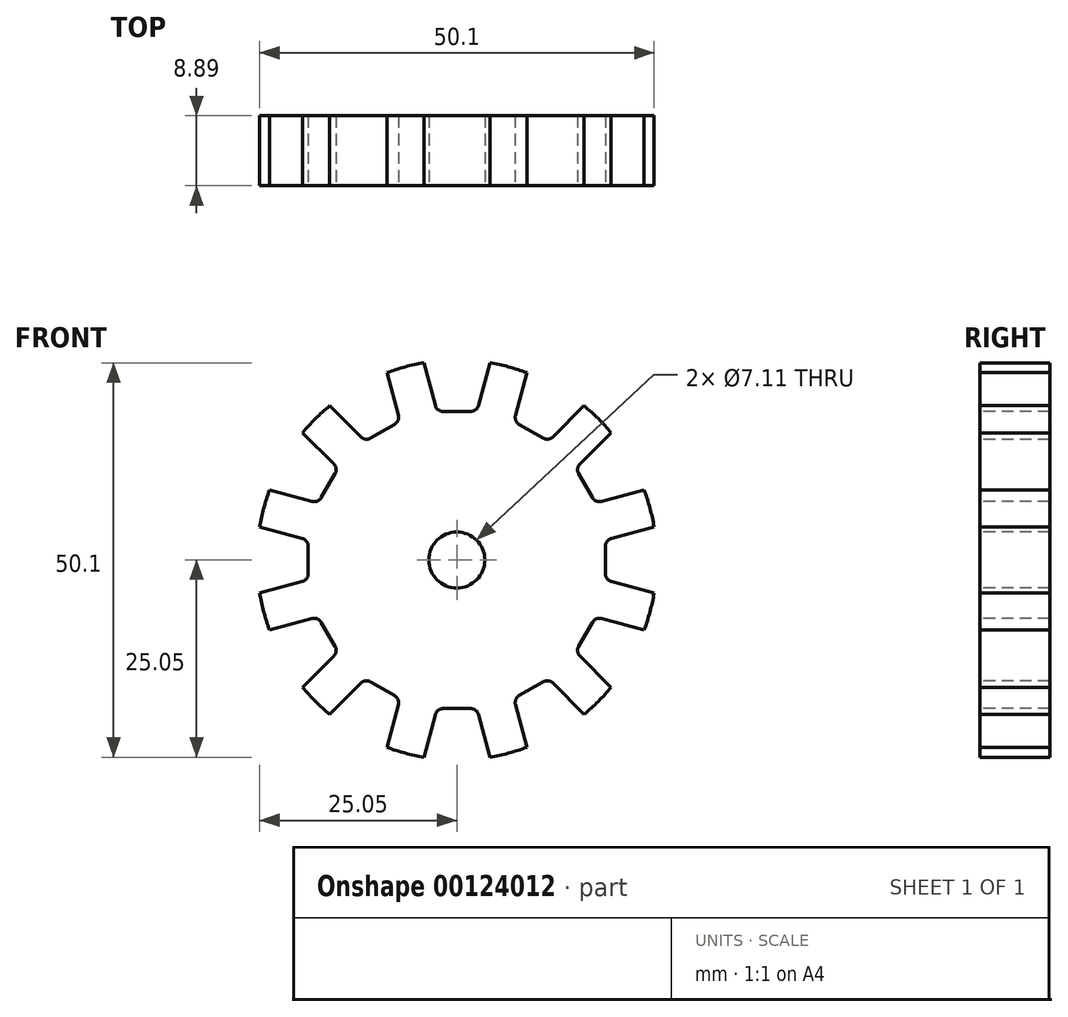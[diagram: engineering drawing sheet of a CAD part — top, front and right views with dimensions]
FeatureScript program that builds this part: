
annotation { "Feature Type Name" : "Feature", "Feature Type Description" : "" }
export const myFeature = defineFeature(function(context is Context, id is Id, definition is map)
    precondition{}
    {
        {
            var Q0;
            Q0=qCreatedBy(makeId("Front.planeOp"),FACE);
            var sketch = newSketch(context, id + "F0", { "sketchPlane" : qUnion([Q0])});
            skCircle(sketch, "E0", {"center": v(0, 0) * mm, "radius": 25.4 * mm});
            skSolve(sketch);
        }
        {
            var Q0;
            Q0 = qSketchRegion(id + "F0", true);
            extrude(context, id + "F1", {"entities" : qUnion([Q0]), "depth" : 8.9 * mm});
        }
        {
            var Q0;
            Q0=makeQuery(id+"F1.opExtrude","CAP_FACE",FACE,{"disambiguationData":[OSD([sQuery(id+"F0.wireOp",EDGE,"E0")])],"isStart":false});
            var sketch = newSketch(context, id + "F2", { "sketchPlane" : qUnion([Q0])});
            skLineSegment(sketch, "E1", {"start": v(0, 0) * mm, "end": v(0, 25.4) * mm, "construction": true});
            skCircle(sketch, "E2", {"center": v(0, 0) * mm, "radius": 19.05 * mm, "construction": true});
            skLineSegment(sketch, "E3", {"start": v(2.74, 19.63) * mm, "end": v(4.2, 25.05) * mm});
            skLineSegment(sketch, "E4", {"start": v(-2.74, 19.63) * mm, "end": v(-4.2, 25.05) * mm});
            skLineSegment(sketch, "E5", {"start": v(-1.76, 18.88) * mm, "end": v(0, 18.88) * mm});
            skLineSegment(sketch, "E6", {"start": v(1.76, 18.88) * mm, "end": v(0, 18.88) * mm});
            skPoint(sketch, "E7.visualSharp", {"position": v(2.54, 18.88) * mm});
            skArc(sketch, "E7.filletArc", {"start": v(1.76, 18.88) * mm, "mid": v(2.38, 19.09) * mm, "end": v(2.74, 19.63) * mm});
            skPoint(sketch, "E8.visualSharp", {"position": v(-2.54, 18.88) * mm});
            skArc(sketch, "E8.filletArc", {"start": v(-2.74, 19.63) * mm, "mid": v(-2.38, 19.09) * mm, "end": v(-1.76, 18.88) * mm});
            skSolve(sketch);
        }
        {
            var Q0;
            {var subQ1=sQuery(id+"F2.wireOp",EDGE,"E3");Q0=makeQuery(id+"F2.imprint","IMPRINT",FACE,{"disambiguationData":[TD([[makeQuery(id+"F2.imprint","IMPRINT",EDGE,{"derivedFrom":subQ1}),1.0]])]});}
            extrude(context, id + "F3", {"entities" : qUnion([Q0]), "operationType" : NewBodyOperationType.REMOVE, "oppositeDirection" : true, "depth" : 25.4 * mm});
        }
        {
            var Q0;
            Q0=makeQuery(id+"F1.opExtrude","SWEPT_BODY",BODY,{"disambiguationData":[OSD([sQuery(id+"F0.wireOp",EDGE,"E0")])]});
            var Q1;
            Q1=makeQuery(id+"F3.boolean.opBoolean","COPY",FACE,{"derivedFrom":makeQuery(id+"F3.opExtrude","SWEPT_FACE",FACE,{"disambiguationData":[OSD([sQuery(id+"F2.wireOp",EDGE,"E4")])]})});
            var Q2;
            Q2=makeQuery(id+"F3.boolean.opBoolean","COPY",FACE,{"derivedFrom":makeQuery(id+"F3.opExtrude","SWEPT_FACE",FACE,{"disambiguationData":[OSD([sQuery(id+"F2.wireOp",EDGE,"E8.filletArc")])]})});
            var Q3;
            Q3=makeQuery(id+"F3.boolean.opBoolean","COPY",FACE,{"derivedFrom":makeQuery(id+"F3.opExtrude","SWEPT_FACE",FACE,{"disambiguationData":[OSD([sQuery(id+"F2.wireOp",EDGE,"E5"),sQuery(id+"F2.wireOp",EDGE,"E6")])]})});
            var Q4;
            Q4=makeQuery(id+"F3.boolean.opBoolean","COPY",FACE,{"derivedFrom":makeQuery(id+"F3.opExtrude","SWEPT_FACE",FACE,{"disambiguationData":[OSD([sQuery(id+"F2.wireOp",EDGE,"E7.filletArc")])]})});
            var Q5;
            Q5=makeQuery(id+"F3.boolean.opBoolean","COPY",FACE,{"derivedFrom":makeQuery(id+"F3.opExtrude","SWEPT_FACE",FACE,{"disambiguationData":[OSD([sQuery(id+"F2.wireOp",EDGE,"E3")])]})});
            var Q6;
            Q6=makeQuery(id+"F1.opExtrude","SWEPT_FACE",FACE,{"disambiguationData":[OSD([sQuery(id+"F0.wireOp",EDGE,"E0")])]});
            circularPattern(context, id + "F4", {"patternType" : PatternType.FACE, "faces" : qUnion([Q1, Q2, Q3, Q4, Q5]), "axis" : qUnion([Q6]), "angle" : 30 * degree, "instanceCount" : 12});
        }
        {
            var Q0;
            Q0=makeQuery(id+"F1.opExtrude","CAP_FACE",FACE,{"disambiguationData":[OSD([sQuery(id+"F0.wireOp",EDGE,"E0")])],"isStart":false});
            var sketch = newSketch(context, id + "F5", { "sketchPlane" : qUnion([Q0])});
            skCircle(sketch, "E9", {"center": v(0, 0) * mm, "radius": 3.56 * mm});
            skSolve(sketch);
        }
        {
            var Q0;
            Q0=makeQuery(id+"F5.imprint","IMPRINT",FACE,{"disambiguationData":[TD([[makeQuery(id+"F5.imprint","IMPRINT",EDGE,{"derivedFrom":sQuery(id+"F5.wireOp",EDGE,"E9")}),1.0]])]});
            extrude(context, id + "F6", {"entities" : qUnion([Q0]), "operationType" : NewBodyOperationType.REMOVE, "oppositeDirection" : true, "depth" : 25.4 * mm});
        }
    });
